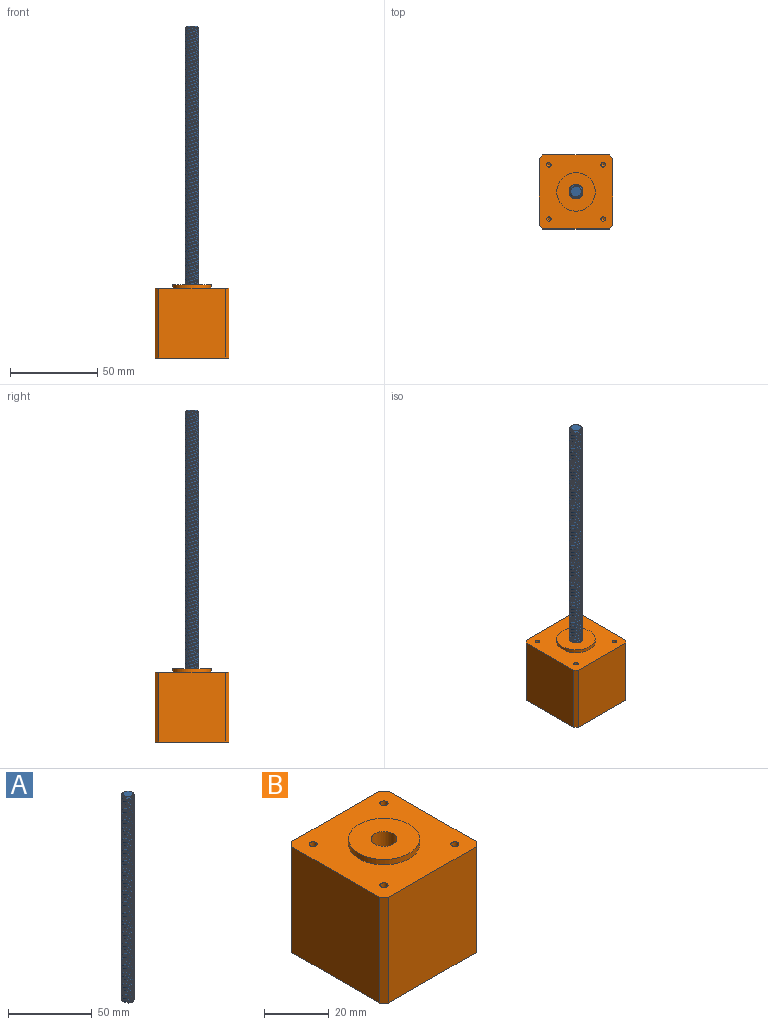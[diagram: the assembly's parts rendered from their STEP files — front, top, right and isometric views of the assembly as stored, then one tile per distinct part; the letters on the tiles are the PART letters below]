
ASSEMBLY  parts=2 mates=1
PART A: 22 faces, bbox 8x8x152 mm
  f0: cylinder r=4mm len=149mm, axis (0,0,-1), area 467.6mm2, adj f1,f9,f10,f20
  f1: plane 8.03x8.03mm, normal (0,0,-1), area 42.2mm2, adj f0,f3,f5,f7,f10,f11,f12,f13
  f2: cone r=3mm half-angle=45deg, axis (0,0,-1), area 4.9mm2, adj f3,f8,f17,f19
  f3: cylinder r=4mm len=149mm, axis (0,0,-1), area 467.6mm2, adj f1,f2,f17,f19
  f4: cone r=3mm half-angle=45deg, axis (0,0,-1), area 4.9mm2, adj f5,f8,f14,f16
  f5: cylinder r=4mm len=149mm, axis (0,0,-1), area 467.6mm2, adj f1,f4,f14,f16
  f6: cone r=3mm half-angle=45deg, axis (0,0,-1), area 4.9mm2, adj f7,f8,f11,f13
  f7: cylinder r=4mm len=149mm, axis (0,0,-1), area 467.6mm2, adj f1,f6,f11,f13
  f8: plane 6x6mm, normal (0,0,1), area 28.3mm2, adj f2,f4,f6,f9,f12,f15,f18,f21
  f9: cone r=3mm half-angle=45deg, axis (0,0,-1), area 4.9mm2, adj f0,f8,f10,f20
  f10: bspline ~151.27x8mm, area 450.8mm2, adj f0,f1,f9,f12
  f11: bspline ~151.27x8mm, area 450.8mm2, adj f1,f6,f7,f12
  f12: cylinder r=3mm len=150mm, axis (0,0,1), area 231.5mm2, adj f1,f8,f10,f11
  f13: bspline ~151.27x8mm, area 450.8mm2, adj f1,f6,f7,f15
  f14: bspline ~151.27x8mm, area 450.8mm2, adj f1,f4,f5,f15
  f15: cylinder r=3mm len=150mm, axis (0,0,1), area 231.5mm2, adj f1,f8,f13,f14
  f16: bspline ~151.27x8mm, area 450.8mm2, adj f1,f4,f5,f18
  f17: bspline ~151.27x8mm, area 450.8mm2, adj f1,f2,f3,f18
  f18: cylinder r=3mm len=150mm, axis (0,0,1), area 231.5mm2, adj f1,f8,f16,f17
  f19: bspline ~151.27x8mm, area 450.8mm2, adj f1,f2,f3,f21
  f20: bspline ~151.27x8mm, area 450.8mm2, adj f0,f1,f9,f21
  f21: cylinder r=3mm len=150mm, axis (0,0,1), area 231.5mm2, adj f1,f8,f19,f20
PART B: 21 faces, bbox 42.3x42.3x42 mm
  f0: plane 40x38.3mm, normal (0,1,0), area 1532mm2, adj f5,f6,f17,f19
  f1: plane 40x38.3mm, normal (-1,0,0), area 1532mm2, adj f5,f6,f17,f18
  f2: plane 40x38.3mm, normal (0,-1,0), area 1532mm2, adj f5,f6,f18,f20
  f3: plane 40x38.3mm, normal (1,0,0), area 1532mm2, adj f5,f6,f19,f20
  f4: cylinder r=4mm len=42mm, axis (0,0,1), area 1055.6mm2, adj f5,f8
  f5: plane 42.3x42.3mm, normal (0,0,-1), area 1731mm2, adj f0,f1,f2,f3,f4,f17,f18,f19
  f6: plane 42.3x42.3mm, normal (0,0,1), area 1381.5mm2, adj f0,f1,f2,f3,f7,f10,f12,f14
  f7: cylinder r=11mm len=22mm, axis (0,0,-1), area 138.2mm2, adj f6,f8
  f8: plane 22x22mm, normal (0,0,1), area 329.9mm2, adj f4,f7
  f9: cone r=0mm half-angle=59deg, axis (0,0,1), area 5.7mm2, adj f10
  f10: cylinder r=1.25mm len=5.5mm, axis (0,0,1), area 43.2mm2, adj f6,f9
  f11: cone r=0mm half-angle=59deg, axis (0,0,1), area 5.7mm2, adj f12
  f12: cylinder r=1.25mm len=5.5mm, axis (0,0,1), area 43.2mm2, adj f6,f11
  f13: cone r=0mm half-angle=59deg, axis (0,0,1), area 5.7mm2, adj f14
  f14: cylinder r=1.25mm len=5.5mm, axis (0,0,1), area 43.2mm2, adj f6,f13
  f15: cone r=0mm half-angle=59deg, axis (0,0,1), area 5.7mm2, adj f16
  f16: cylinder r=1.25mm len=5.5mm, axis (0,0,1), area 43.2mm2, adj f6,f15
  f17: plane 40x2mm, normal (-0.71,0.71,0), area 113.1mm2, adj f0,f1,f5,f6
  f18: plane 40x2mm, normal (-0.71,-0.71,0), area 113.1mm2, adj f1,f2,f5,f6
  f19: plane 40x2mm, normal (0.71,0.71,0), area 113.1mm2, adj f0,f3,f5,f6
  f20: plane 40x2mm, normal (0.71,-0.71,0), area 113.1mm2, adj f2,f3,f5,f6
PLACE A at identity
PLACE B at identity fixed
MATE revolute A.f0 <-> B.f7  axis (0,0,-1) through (0,0,0)mm
